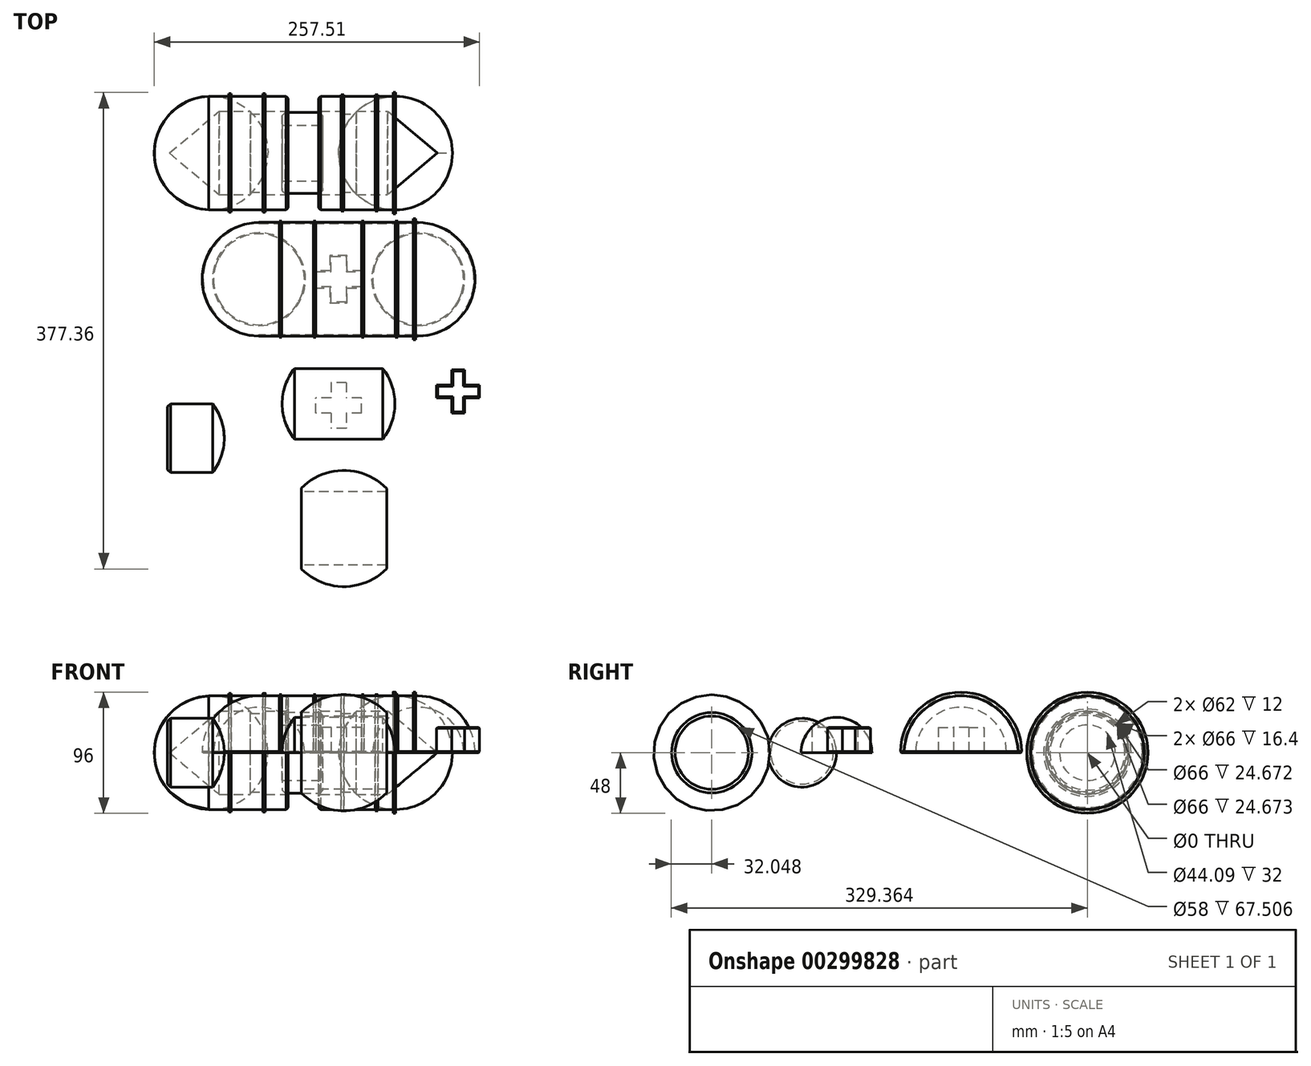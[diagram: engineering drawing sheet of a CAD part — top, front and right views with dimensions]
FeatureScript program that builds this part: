
annotation { "Feature Type Name" : "Feature", "Feature Type Description" : "" }
export const myFeature = defineFeature(function(context is Context, id is Id, definition is map)
    precondition{}
    {
        {
            var Q0;
            Q0=qCreatedBy(makeId("Top.planeOp"),FACE);
            var sketch = newSketch(context, id + "F0", { "sketchPlane" : qUnion([Q0])});
            skLineSegment(sketch, "E0", {"start": v(0, 0) * mm, "end": v(0, 70) * mm});
            skLineSegment(sketch, "E1.left", {"start": v(63, 50) * mm, "end": v(63, 95) * mm});
            skArc(sketch, "E2", {"start": v(108, 50) * mm, "mid": v(94.82, 81.82) * mm, "end": v(63, 95) * mm});
            skLineSegment(sketch, "E3", {"start": v(99, 50) * mm, "end": v(108, 50) * mm});
            skLineSegment(sketch, "E4.left", {"start": v(45, 95) * mm, "end": v(45, 96) * mm});
            skLineSegment(sketch, "E4.right", {"start": v(47, 95) * mm, "end": v(47, 96) * mm});
            skLineSegment(sketch, "E5.top", {"start": v(18, 96) * mm, "end": v(20, 96) * mm});
            skLineSegment(sketch, "E5.left", {"start": v(18, 95) * mm, "end": v(18, 96) * mm});
            skLineSegment(sketch, "E5.right", {"start": v(20, 95) * mm, "end": v(20, 96) * mm});
            skLineSegment(sketch, "E6", {"start": v(20, 95) * mm, "end": v(45, 95) * mm});
            skLineSegment(sketch, "E7", {"start": v(27, 50) * mm, "end": v(0, 50) * mm});
            skLineSegment(sketch, "E8.top", {"start": v(59, 98) * mm, "end": v(61, 98) * mm});
            skLineSegment(sketch, "E8.left", {"start": v(59, 95) * mm, "end": v(59, 98) * mm});
            skLineSegment(sketch, "E8.right", {"start": v(61, 95) * mm, "end": v(61, 98) * mm});
            skLineSegment(sketch, "E9", {"start": v(47, 95) * mm, "end": v(59, 95) * mm});
            skLineSegment(sketch, "E10", {"start": v(61, 95) * mm, "end": v(63, 95) * mm});
            skLineSegment(sketch, "E11", {"start": v(18, 95) * mm, "end": v(0, 95) * mm});
            skLineSegment(sketch, "E12", {"start": v(45, 96) * mm, "end": v(47, 96) * mm});
            skLineSegment(sketch, "E13", {"start": v(0, 70) * mm, "end": v(0, 95) * mm});
            skArc(sketch, "E14", {"start": v(99, 50) * mm, "mid": v(63, 86) * mm, "end": v(27, 50) * mm});
            skLineSegment(sketch, "E15.MirrorCS", {"start": v(-61, 95) * mm, "end": v(-63, 95) * mm});
            skLineSegment(sketch, "E16.MirrorCS", {"start": v(-45, 95) * mm, "end": v(-45, 96) * mm});
            skLineSegment(sketch, "E17.MirrorCS", {"start": v(-18, 96) * mm, "end": v(-20, 96) * mm});
            skLineSegment(sketch, "E18.MirrorCS", {"start": v(-18, 95) * mm, "end": v(-18, 96) * mm});
            skLineSegment(sketch, "E19.MirrorCS", {"start": v(-20, 95) * mm, "end": v(-20, 96) * mm});
            skLineSegment(sketch, "E20.MirrorCS", {"start": v(-45, 96) * mm, "end": v(-47, 96) * mm});
            skLineSegment(sketch, "E21.MirrorCS", {"start": v(-47, 95) * mm, "end": v(-47, 96) * mm});
            skLineSegment(sketch, "E22.MirrorCS", {"start": v(-99, 50) * mm, "end": v(-108, 50) * mm});
            skLineSegment(sketch, "E23.MirrorCS", {"start": v(-47, 95) * mm, "end": v(-59, 95) * mm});
            skArc(sketch, "E24.MirrorCS", {"start": v(-99, 50) * mm, "mid": v(-63, 86) * mm, "end": v(-27, 50) * mm});
            skLineSegment(sketch, "E25.MirrorCS", {"start": v(-63, 50) * mm, "end": v(-63, 95) * mm});
            skArc(sketch, "E26.MirrorCS", {"start": v(-108, 50) * mm, "mid": v(-94.82, 81.82) * mm, "end": v(-63, 95) * mm});
            skLineSegment(sketch, "E27.MirrorCS", {"start": v(-20, 95) * mm, "end": v(-45, 95) * mm});
            skLineSegment(sketch, "E28.MirrorCS", {"start": v(-18, 95) * mm, "end": v(0, 95) * mm});
            skLineSegment(sketch, "E29.MirrorCS", {"start": v(-27, 50) * mm, "end": v(0, 50) * mm});
            skLineSegment(sketch, "E30", {"start": v(-61, 95) * mm, "end": v(-59, 95) * mm});
            skSolve(sketch);
        }
        {
            var Q0;
            Q0 = qSketchRegion(id + "F0", true);
            var Q1;
            Q1=sQuery(id+"F0.wireOp",EDGE,"E7");
            revolve(context, id + "F1", {"entities" : qUnion([Q0]), "axis" : qUnion([Q1]), "revolveType" : RevolveType.ONE_DIRECTION, "oppositeDirection" : true, "angle" : 180 * degree});
        }
        {
            var Q0;
            Q0=qCreatedBy(makeId("Top.planeOp"),FACE);
            var sketch = newSketch(context, id + "F2", { "sketchPlane" : qUnion([Q0])});
            skArc(sketch, "E31", {"start": v(44.62, -48.6) * mm, "mid": v(42.1, -33.78) * mm, "end": v(34.85, -20.6) * mm});
            skLineSegment(sketch, "E32", {"start": v(34.85, -20.6) * mm, "end": v(0, -20.6) * mm});
            skLineSegment(sketch, "E33", {"start": v(0, 0) * mm, "end": v(0, -20.6) * mm});
            skLineSegment(sketch, "E34", {"start": v(-0.38, -48.6) * mm, "end": v(44.62, -48.6) * mm});
            skLineSegment(sketch, "E35.MirrorCS", {"start": v(-34.85, -20.6) * mm, "end": v(0, -20.6) * mm});
            skArc(sketch, "E36.MirrorCS", {"start": v(-44.62, -48.6) * mm, "mid": v(-42.1, -33.78) * mm, "end": v(-34.85, -20.6) * mm});
            skLineSegment(sketch, "E37.MirrorCS", {"start": v(0.38, -48.6) * mm, "end": v(-44.62, -48.6) * mm});
            skSolve(sketch);
        }
        {
            var Q0;
            Q0 = qSketchRegion(id + "F2", true);
            var Q1;
            Q1=sQuery(id+"F2.wireOp",EDGE,"E34");
            revolve(context, id + "F3", {"entities" : qUnion([Q0]), "axis" : qUnion([Q1]), "revolveType" : RevolveType.ONE_DIRECTION, "angle" : 180 * degree});
        }
        {
            var Q0;
            Q0=qCreatedBy(makeId("Top.planeOp"),FACE);
            var sketch = newSketch(context, id + "F4", { "sketchPlane" : qUnion([Q0])});
            skLineSegment(sketch, "E38", {"start": v(0, 0) * mm, "end": v(0, 50) * mm});
            skLineSegment(sketch, "E39", {"start": v(0, 0) * mm, "end": v(0, -50) * mm});
            skLineSegment(sketch, "E40.bottom", {"start": v(6, -32) * mm, "end": v(-6, -32) * mm});
            skLineSegment(sketch, "E40.top", {"start": v(6, -68) * mm, "end": v(-6, -68) * mm});
            skLineSegment(sketch, "E40.left", {"start": v(6, -32) * mm, "end": v(6, -68) * mm});
            skLineSegment(sketch, "E40.right", {"start": v(-6, -32) * mm, "end": v(-6, -68) * mm});
            skPoint(sketch, "E40.middle", {"position": v(0, -50) * mm});
            skLineSegment(sketch, "E41.bottom", {"start": v(18, -56) * mm, "end": v(-18, -56) * mm});
            skLineSegment(sketch, "E41.top", {"start": v(18, -44) * mm, "end": v(-18, -44) * mm});
            skLineSegment(sketch, "E41.left", {"start": v(18, -56) * mm, "end": v(18, -44) * mm});
            skLineSegment(sketch, "E41.right", {"start": v(-18, -56) * mm, "end": v(-18, -44) * mm});
            skPoint(sketch, "E42.MirrorP", {"position": v(0, 50) * mm});
            skLineSegment(sketch, "E43.MirrorCS", {"start": v(18, 56) * mm, "end": v(18, 44) * mm});
            skLineSegment(sketch, "E44.MirrorCS", {"start": v(-6, 32) * mm, "end": v(-6, 68) * mm});
            skLineSegment(sketch, "E45.MirrorCS", {"start": v(18, 44) * mm, "end": v(-18, 44) * mm});
            skLineSegment(sketch, "E46.MirrorCS", {"start": v(18, 56) * mm, "end": v(-18, 56) * mm});
            skLineSegment(sketch, "E47.MirrorCS", {"start": v(6, 68) * mm, "end": v(-6, 68) * mm});
            skLineSegment(sketch, "E48.MirrorCS", {"start": v(-18, 56) * mm, "end": v(-18, 44) * mm});
            skLineSegment(sketch, "E49.MirrorCS", {"start": v(6, 32) * mm, "end": v(6, 68) * mm});
            skLineSegment(sketch, "E50.MirrorCS", {"start": v(6, 32) * mm, "end": v(-6, 32) * mm});
            skSolve(sketch);
        }
        {
            var Q0;
            Q0 = qSketchRegion(id + "F4", true);
            extrude(context, id + "F5", {"entities" : qUnion([Q0]), "operationType" : NewBodyOperationType.REMOVE, "depth" : 20 * mm});
        }
        {
            var Q0;
            Q0=qCreatedBy(makeId("Top.planeOp"),FACE);
            var sketch = newSketch(context, id + "F6", { "sketchPlane" : qUnion([Q0])});
            skArc(sketch, "E51", {"start": v(38.11, -118.35) * mm, "mid": v(4.36, -102.85) * mm, "end": v(-29.4, -118.35) * mm});
            skLineSegment(sketch, "E52", {"start": v(4.36, -147.35) * mm, "end": v(48.86, -147.35) * mm});
            skArc(sketch, "E53", {"start": v(38.11, -115.56) * mm, "mid": v(4.41, -101.35) * mm, "end": v(-29.4, -115.3) * mm});
            skLineSegment(sketch, "E54", {"start": v(38.11, -118.35) * mm, "end": v(38.11, -115.56) * mm});
            skLineSegment(sketch, "E55.MirrorCS", {"start": v(-29.4, -118.35) * mm, "end": v(-29.4, -115.3) * mm});
            skLineSegment(sketch, "E56", {"start": v(38.11, -118.35) * mm, "end": v(-29.4, -118.35) * mm});
            skLineSegment(sketch, "E57", {"start": v(4.36, -147.35) * mm, "end": v(4.36, -118.35) * mm});
            skSolve(sketch);
        }
        {
            var Q0;
            Q0 = qSketchRegion(id + "F6", true);
            var Q1;
            Q1=sQuery(id+"F6.wireOp",EDGE,"E52");
            revolve(context, id + "F7", {"entities" : qUnion([Q0]), "axis" : qUnion([Q1]), "revolveType" : RevolveType.FULL});
        }
        {
            var Q0;
            Q0=qCreatedBy(makeId("Top.planeOp"),FACE);
            var sketch = newSketch(context, id + "F8", { "sketchPlane" : qUnion([Q0])});
            skLineSegment(sketch, "E58.bottom", {"start": v(111.61, -43.86) * mm, "end": v(77.61, -43.86) * mm});
            skLineSegment(sketch, "E58.top", {"start": v(111.61, -33.86) * mm, "end": v(77.61, -33.86) * mm});
            skLineSegment(sketch, "E58.left", {"start": v(111.61, -43.86) * mm, "end": v(111.61, -33.86) * mm});
            skLineSegment(sketch, "E58.right", {"start": v(77.61, -43.86) * mm, "end": v(77.61, -33.86) * mm});
            skPoint(sketch, "E58.middle", {"position": v(94.61, -38.86) * mm});
            skLineSegment(sketch, "E59.bottom", {"start": v(99.61, -55.86) * mm, "end": v(89.61, -55.86) * mm});
            skLineSegment(sketch, "E59.top", {"start": v(99.61, -21.86) * mm, "end": v(89.61, -21.86) * mm});
            skLineSegment(sketch, "E59.left", {"start": v(99.61, -55.86) * mm, "end": v(99.61, -21.86) * mm});
            skLineSegment(sketch, "E59.right", {"start": v(89.61, -55.86) * mm, "end": v(89.61, -21.86) * mm});
            skSolve(sketch);
        }
        {
            var Q0;
            Q0 = qSketchRegion(id + "F8", true);
            extrude(context, id + "F9", {"entities" : qUnion([Q0]), "depth" : 20 * mm, "offsetDistance" : 25 * mm});
        }
        {
            var Q0;
            Q0=makeQuery(id+"F3.opRevolve","CAP_FACE",FACE,{"disambiguationData":[OSD([sQuery(id+"F2.wireOp",EDGE,"E31"),sQuery(id+"F2.wireOp",EDGE,"E32"),sQuery(id+"F2.wireOp",EDGE,"E34"),sQuery(id+"F2.wireOp",EDGE,"E35.MirrorCS"),sQuery(id+"F2.wireOp",EDGE,"E36.MirrorCS"),sQuery(id+"F2.wireOp",EDGE,"E37.MirrorCS")])],"isStart":true});
            var Q1;
            Q1=makeQuery(id+"F1.opRevolve","CAP_FACE",FACE,{"disambiguationData":[OSD([sQuery(id+"F0.wireOp",EDGE,"E2"),sQuery(id+"F0.wireOp",EDGE,"E3"),sQuery(id+"F0.wireOp",EDGE,"E4.left"),sQuery(id+"F0.wireOp",EDGE,"E4.right"),sQuery(id+"F0.wireOp",EDGE,"E5.top"),sQuery(id+"F0.wireOp",EDGE,"E5.left"),sQuery(id+"F0.wireOp",EDGE,"E5.right"),sQuery(id+"F0.wireOp",EDGE,"E6"),sQuery(id+"F0.wireOp",EDGE,"E7"),sQuery(id+"F0.wireOp",EDGE,"E8.top"),sQuery(id+"F0.wireOp",EDGE,"E8.left"),sQuery(id+"F0.wireOp",EDGE,"E8.right"),sQuery(id+"F0.wireOp",EDGE,"E9"),sQuery(id+"F0.wireOp",EDGE,"E10"),sQuery(id+"F0.wireOp",EDGE,"E11"),sQuery(id+"F0.wireOp",EDGE,"E12"),sQuery(id+"F0.wireOp",EDGE,"E14"),sQuery(id+"F0.wireOp",EDGE,"E15.MirrorCS"),sQuery(id+"F0.wireOp",EDGE,"E16.MirrorCS"),sQuery(id+"F0.wireOp",EDGE,"E17.MirrorCS"),sQuery(id+"F0.wireOp",EDGE,"E18.MirrorCS"),sQuery(id+"F0.wireOp",EDGE,"E19.MirrorCS"),sQuery(id+"F0.wireOp",EDGE,"E20.MirrorCS"),sQuery(id+"F0.wireOp",EDGE,"E21.MirrorCS"),sQuery(id+"F0.wireOp",EDGE,"E22.MirrorCS"),sQuery(id+"F0.wireOp",EDGE,"E23.MirrorCS"),sQuery(id+"F0.wireOp",EDGE,"E24.MirrorCS"),sQuery(id+"F0.wireOp",EDGE,"E26.MirrorCS"),sQuery(id+"F0.wireOp",EDGE,"E27.MirrorCS"),sQuery(id+"F0.wireOp",EDGE,"E28.MirrorCS"),sQuery(id+"F0.wireOp",EDGE,"E29.MirrorCS"),sQuery(id+"F0.wireOp",EDGE,"E30")])],"isStart":true});
            var Q2;
            Q2=makeQuery(id+"F9.opExtrude","CAP_FACE",FACE,{"disambiguationData":[OSD([sQuery(id+"F8.wireOp",EDGE,"E58.bottom"),sQuery(id+"F8.wireOp",EDGE,"E58.top"),sQuery(id+"F8.wireOp",EDGE,"E58.left"),sQuery(id+"F8.wireOp",EDGE,"E58.right"),sQuery(id+"F8.wireOp",EDGE,"E59.bottom"),sQuery(id+"F8.wireOp",EDGE,"E59.top"),sQuery(id+"F8.wireOp",EDGE,"E59.left"),sQuery(id+"F8.wireOp",EDGE,"E59.right")])],"isStart":true});
            var Q3;
            Q3=makeQuery(id+"F9.opExtrude","CAP_FACE",FACE,{"disambiguationData":[OSD([sQuery(id+"F8.wireOp",EDGE,"E58.bottom"),sQuery(id+"F8.wireOp",EDGE,"E58.top"),sQuery(id+"F8.wireOp",EDGE,"E58.left"),sQuery(id+"F8.wireOp",EDGE,"E58.right"),sQuery(id+"F8.wireOp",EDGE,"E59.bottom"),sQuery(id+"F8.wireOp",EDGE,"E59.top"),sQuery(id+"F8.wireOp",EDGE,"E59.left"),sQuery(id+"F8.wireOp",EDGE,"E59.right")])],"isStart":false});
            chamfer(context, id + "F10", {"entities" : qUnion([Q0, Q1, Q2, Q3]), "width" : .8 * mm, "tangentPropagation" : true});
        }
        {
            var Q0;
            Q0=qCreatedBy(makeId("Top.planeOp"),FACE);
            var sketch = newSketch(context, id + "F11", { "sketchPlane" : qUnion([Q0])});
            skLineSegment(sketch, "E60.MirrorCS", {"start": v(-100.99, 194.96) * mm, "end": v(-102.9, 194.96) * mm});
            skLineSegment(sketch, "E61.MirrorCS", {"start": v(-84.9, 194.96) * mm, "end": v(-84.9, 196.96) * mm});
            skLineSegment(sketch, "E62.MirrorCS", {"start": v(-57.99, 196.96) * mm, "end": v(-59.9, 196.96) * mm});
            skLineSegment(sketch, "E63.MirrorCS", {"start": v(-57.99, 194.96) * mm, "end": v(-57.99, 196.96) * mm});
            skLineSegment(sketch, "E64.MirrorCS", {"start": v(-59.9, 194.96) * mm, "end": v(-59.9, 196.96) * mm});
            skLineSegment(sketch, "E65.MirrorCS", {"start": v(-84.9, 196.96) * mm, "end": v(-86.9, 196.96) * mm});
            skLineSegment(sketch, "E66.MirrorCS", {"start": v(-86.9, 194.96) * mm, "end": v(-86.9, 196.96) * mm});
            skLineSegment(sketch, "E67.MirrorCS", {"start": v(-86.9, 194.96) * mm, "end": v(-98.9, 194.96) * mm});
            skArc(sketch, "E68.MirrorCS", {"start": v(-145.9, 149.96) * mm, "mid": v(-133.43, 181.1) * mm, "end": v(-102.9, 194.96) * mm});
            skLineSegment(sketch, "E69.MirrorCS", {"start": v(-59.9, 194.96) * mm, "end": v(-84.9, 194.96) * mm});
            skLineSegment(sketch, "E70.MirrorCS", {"start": v(-57.99, 194.96) * mm, "end": v(-39.9, 194.96) * mm});
            skLineSegment(sketch, "E71", {"start": v(-100.99, 194.96) * mm, "end": v(-98.9, 194.96) * mm});
            skLineSegment(sketch, "E72", {"start": v(-133.9, 149.96) * mm, "end": v(-145.9, 149.96) * mm});
            skLineSegment(sketch, "E73", {"start": v(-133.9, 149.96) * mm, "end": v(-94.57, 182.96) * mm});
            skArc(sketch, "E74", {"start": v(90.1, 149.96) * mm, "mid": v(76.92, 181.78) * mm, "end": v(45.1, 194.96) * mm});
            skLineSegment(sketch, "E75.left", {"start": v(29.1, 194.96) * mm, "end": v(29.1, 195.96) * mm});
            skLineSegment(sketch, "E75.right", {"start": v(31.1, 194.96) * mm, "end": v(31.1, 195.96) * mm});
            skLineSegment(sketch, "E76.top", {"start": v(2.1, 195.96) * mm, "end": v(4.1, 195.96) * mm});
            skLineSegment(sketch, "E76.left", {"start": v(2.1, 194.96) * mm, "end": v(2.1, 195.96) * mm});
            skLineSegment(sketch, "E76.right", {"start": v(4.1, 194.96) * mm, "end": v(4.1, 195.96) * mm});
            skLineSegment(sketch, "E77", {"start": v(4.1, 194.96) * mm, "end": v(29.1, 194.96) * mm});
            skLineSegment(sketch, "E78.top", {"start": v(43.1, 197.96) * mm, "end": v(45.1, 197.96) * mm});
            skLineSegment(sketch, "E78.left", {"start": v(43.1, 194.96) * mm, "end": v(43.1, 197.96) * mm});
            skLineSegment(sketch, "E78.right", {"start": v(45.1, 194.96) * mm, "end": v(45.1, 197.96) * mm});
            skLineSegment(sketch, "E79", {"start": v(31.1, 194.96) * mm, "end": v(43.1, 194.96) * mm});
            skLineSegment(sketch, "E80", {"start": v(45.1, 194.96) * mm, "end": v(45.1, 194.96) * mm});
            skLineSegment(sketch, "E81", {"start": v(2.1, 194.96) * mm, "end": v(-15.9, 194.96) * mm});
            skLineSegment(sketch, "E82", {"start": v(29.1, 195.96) * mm, "end": v(31.1, 195.96) * mm});
            skLineSegment(sketch, "E83", {"start": v(-39.9, 194.96) * mm, "end": v(-39.9, 182.96) * mm});
            skLineSegment(sketch, "E84", {"start": v(-94.57, 182.96) * mm, "end": v(-39.9, 182.96) * mm});
            skLineSegment(sketch, "E85", {"start": v(-15.9, 182.96) * mm, "end": v(-15.9, 194.96) * mm});
            skLineSegment(sketch, "E86", {"start": v(-15.9, 182.96) * mm, "end": v(38.77, 182.96) * mm});
            skLineSegment(sketch, "E87", {"start": v(38.77, 182.96) * mm, "end": v(78.1, 149.96) * mm});
            skLineSegment(sketch, "E88", {"start": v(78.1, 149.96) * mm, "end": v(90.1, 149.96) * mm});
            skLineSegment(sketch, "E89.bottom", {"start": v(-44.56, 182) * mm, "end": v(-12.56, 182) * mm});
            skLineSegment(sketch, "E89.top", {"start": v(-44.56, 172) * mm, "end": v(-12.56, 172) * mm});
            skLineSegment(sketch, "E89.left", {"start": v(-44.56, 182) * mm, "end": v(-44.56, 172) * mm});
            skLineSegment(sketch, "E89.right", {"start": v(-12.56, 182) * mm, "end": v(-12.56, 172) * mm});
            skLineSegment(sketch, "E90.bottom", {"start": v(-69.9, 182.96) * mm, "end": v(-57.9, 182.96) * mm});
            skLineSegment(sketch, "E90.top", {"start": v(-69.9, 180.96) * mm, "end": v(-57.9, 180.96) * mm});
            skLineSegment(sketch, "E90.left", {"start": v(-69.9, 182.96) * mm, "end": v(-69.9, 180.96) * mm});
            skLineSegment(sketch, "E90.right", {"start": v(-57.9, 182.96) * mm, "end": v(-57.9, 180.96) * mm});
            skLineSegment(sketch, "E91.bottom", {"start": v(2.1, 182.96) * mm, "end": v(14.1, 182.96) * mm});
            skLineSegment(sketch, "E91.top", {"start": v(2.1, 180.96) * mm, "end": v(14.1, 180.96) * mm});
            skLineSegment(sketch, "E91.left", {"start": v(2.1, 182.96) * mm, "end": v(2.1, 180.96) * mm});
            skLineSegment(sketch, "E91.right", {"start": v(14.1, 182.96) * mm, "end": v(14.1, 180.96) * mm});
            skSolve(sketch);
        }
        {
            var Q0;
            Q0 = qSketchRegion(id + "F11", true);
            var Q1;
            Q1=sQuery(id+"F11.wireOp",EDGE,"E72");
            revolve(context, id + "F12", {"surfaceOperationType" : NewSurfaceOperationType.NEW, "entities" : qUnion([Q0]), "axis" : qUnion([Q1]), "revolveType" : RevolveType.FULL});
        }
        {
            var Q0;
            Q0=makeQuery(id+"F12.opRevolve","SWEPT_FACE",FACE,{"disambiguationData":[OSD([sQuery(id+"F11.wireOp",EDGE,"E83")])]});
            var Q1;
            Q1=makeQuery(id+"F12.opRevolve","SWEPT_FACE",FACE,{"disambiguationData":[OSD([sQuery(id+"F11.wireOp",EDGE,"E85")])]});
            chamfer(context, id + "F13", {"entities" : qUnion([Q0, Q1]), "width" : 1.6 * mm, "tangentPropagation" : true});
        }
        {
            var Q0;
            Q0=qCreatedBy(makeId("Top.planeOp"),FACE);
            var sketch = newSketch(context, id + "F14", { "sketchPlane" : qUnion([Q0])});
            skArc(sketch, "E92", {"start": v(-90.52, -75.86) * mm, "mid": v(-92.86, -61.5) * mm, "end": v(-99.67, -48.66) * mm});
            skLineSegment(sketch, "E93", {"start": v(-99.67, -48.66) * mm, "end": v(-135.52, -48.66) * mm});
            skLineSegment(sketch, "E94", {"start": v(-135.52, -75.86) * mm, "end": v(-90.52, -75.86) * mm});
            skLineSegment(sketch, "E95", {"start": v(-135.52, -48.66) * mm, "end": v(-135.52, -75.86) * mm});
            skSolve(sketch);
        }
        {
            var Q0;
            Q0 = qSketchRegion(id + "F14", true);
            var Q1;
            Q1=sQuery(id+"F14.wireOp",EDGE,"E94");
            revolve(context, id + "F15", {"surfaceOperationType" : NewSurfaceOperationType.NEW, "entities" : qUnion([Q0]), "axis" : qUnion([Q1]), "revolveType" : RevolveType.FULL});
        }
        {
            var Q0;
            Q0=makeQuery(id+"F15.opRevolve","SWEPT_EDGE",EDGE,{"disambiguationData":[OSD([sQuery(id+"F14.wireOp",EDGE,"E93"),sQuery(id+"F14.wireOp",EDGE,"E95")])]});
            chamfer(context, id + "F16", {"entities" : qUnion([Q0]), "width" : 2.4 * mm, "tangentPropagation" : true});
        }
        {
            var Q0;
            Q0=makeQuery(id+"F12.opRevolve","SWEPT_EDGE",EDGE,{"disambiguationData":[OSD([sQuery(id+"F11.wireOp",EDGE,"E89.bottom"),sQuery(id+"F11.wireOp",EDGE,"E89.right")])]});
            var Q1;
            Q1=makeQuery(id+"F12.opRevolve","SWEPT_EDGE",EDGE,{"disambiguationData":[OSD([sQuery(id+"F11.wireOp",EDGE,"E89.bottom"),sQuery(id+"F11.wireOp",EDGE,"E89.left")])]});
            chamfer(context, id + "F17", {"entities" : qUnion([Q0, Q1]), "width" : 2.4 * mm, "tangentPropagation" : true});
        }
    });
